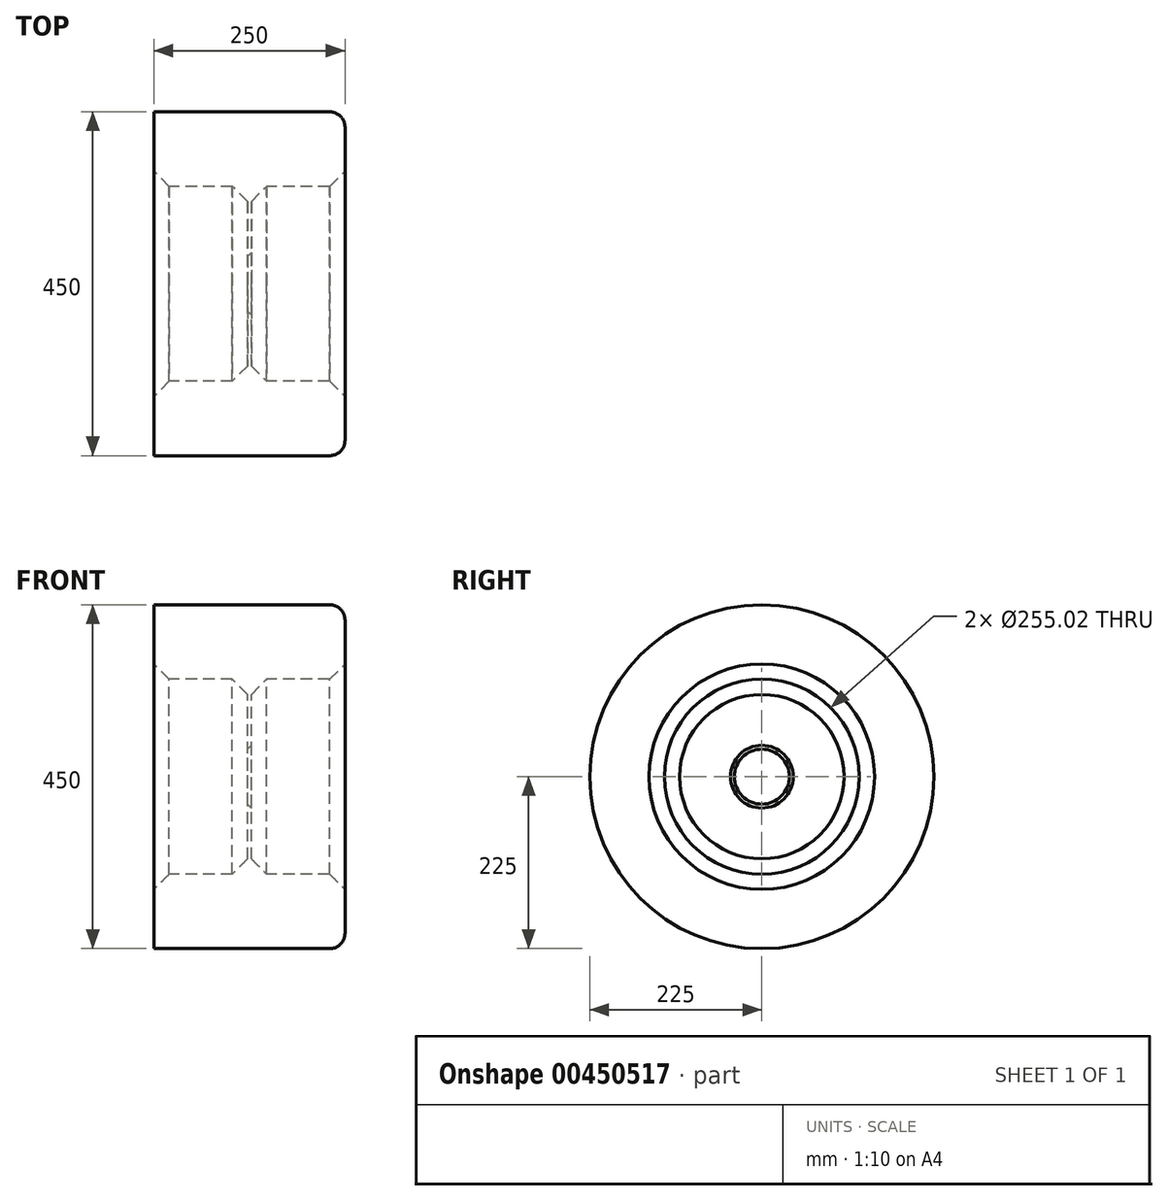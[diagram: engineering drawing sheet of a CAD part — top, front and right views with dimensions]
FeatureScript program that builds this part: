
annotation { "Feature Type Name" : "Feature", "Feature Type Description" : "" }
export const myFeature = defineFeature(function(context is Context, id is Id, definition is map)
    precondition{}
    {
        {
            var Q0;
            Q0=qCreatedBy(makeId("Right.planeOp"),FACE);
            var sketch = newSketch(context, id + "F0", { "sketchPlane" : qUnion([Q0])});
            skCircle(sketch, "E0", {"center": v(0, 0) * mm, "radius": 225 * mm});
            skCircle(sketch, "E1", {"center": v(0, 0) * mm, "radius": 127.5 * mm});
            skCircle(sketch, "E2", {"center": v(0, 0) * mm, "radius": 21 * mm});
            skSolve(sketch);
        }
        {
            var Q0;
            Q0=makeQuery(id+"F0.imprint","IMPRINT",FACE,{"disambiguationData":[TD([[makeQuery(id+"F0.imprint","IMPRINT",EDGE,{"derivedFrom":sQuery(id+"F0.wireOp",EDGE,"E0")}),1.0]])]});
            extrude(context, id + "F1", {"entities" : qUnion([Q0]), "endBound" : BoundingType.SYMMETRIC, "depth" : 250 * mm});
        }
        {
            var Q0;
            Q0=makeQuery(id+"F0.imprint","IMPRINT",FACE,{"disambiguationData":[TD([[makeQuery(id+"F0.imprint","IMPRINT",EDGE,{"derivedFrom":sQuery(id+"F0.wireOp",EDGE,"E1")}),1.0]])]});
            extrude(context, id + "F2", {"entities" : qUnion([Q0]), "operationType" : NewBodyOperationType.ADD, "endBound" : BoundingType.SYMMETRIC, "depth" : 5 * mm});
        }
        {
            var Q0;
            Q0=makeQuery(id+"F1.opExtrude","CAP_EDGE",EDGE,{"disambiguationData":[OSD([sQuery(id+"F0.wireOp",EDGE,"E0")])],"isStart":false});
            fillet(context, id + "F3", {"entities" : qUnion([Q0]), "radius" : 20 * mm, "tangentPropagation" : true, "allowEdgeOverflow" : false});
        }
        {
            var Q0;
            Q0=makeQuery(id+"F1.opExtrude","CAP_EDGE",EDGE,{"disambiguationData":[OSD([sQuery(id+"F0.wireOp",EDGE,"E1")])],"isStart":true});
            var Q1;
            Q1=makeQuery(id+"F2.opExtrude","CAP_EDGE",EDGE,{"disambiguationData":[OSD([sQuery(id+"F0.wireOp",EDGE,"E1")])],"isStart":true});
            var Q2;
            Q2=makeQuery(id+"F1.opExtrude","CAP_EDGE",EDGE,{"disambiguationData":[OSD([sQuery(id+"F0.wireOp",EDGE,"E1")])],"isStart":false});
            var Q3;
            Q3=makeQuery(id+"F2.opExtrude","CAP_FACE",FACE,{"disambiguationData":[OSD([sQuery(id+"F0.wireOp",EDGE,"E1"),sQuery(id+"F0.wireOp",EDGE,"E2")])],"isStart":false});
            chamfer(context, id + "F4", {"entities" : qUnion([Q0, Q1, Q2, Q3]), "width" : 20 * mm, "tangentPropagation" : true});
        }
    });
